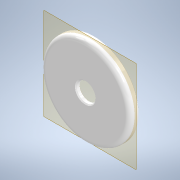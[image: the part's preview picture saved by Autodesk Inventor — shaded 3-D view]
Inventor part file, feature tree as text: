
AUTODESK INVENTOR PART (.ipt)
format: ipt  version: 2021 (Build 250183000, 183)  size: 140,800 bytes
history: native  units: mm
features: other x5, extrude x2, chamfer x2, sketch x2, fillet x1, reference x1
ambient origin geometry x8: Origin, YZ Plane, XZ Plane, XY Plane, X Axis, Y Axis, Z Axis, Center Point
bodies: Body1 (feature_tree)
feature tree (13):
  other  "Bryła1"
  extrude  "Wyciągnięcie proste1"  Depth=190.0mm
  other  "Płaszczyzna konstrukcyjna1"
  extrude  "Wyciągnięcie proste2"  Depth=10.0mm TaperAngle=0.0deg
  fillet  "Zaokrąglenie1"  Radius=40.0mm
  chamfer  "Faza1"  Distance=10.0mm
  chamfer  "Faza2"  Distance=10.0mm
  sketch  "Szkic1"
  reference  "Odniesienie1"
  sketch  "Szkic2"
  other  "Zespół1"
  other  "garnek:1"
  other  "dekiel:1"
